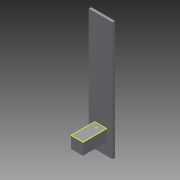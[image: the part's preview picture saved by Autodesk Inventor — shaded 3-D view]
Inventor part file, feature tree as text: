
AUTODESK INVENTOR PART (.ipt)
format: ipt  version: 2014 SP1 (Build 180222100, 222)  size: 95,232 bytes
history: native  units: in
note: dims shown in document units (in); Inventor stores cm internally (conversion verified against a paired STEP export)
features: sketch x4, extrude x2, hole x2
ambient origin geometry x8: Origin, YZ Plane, XZ Plane, XY Plane, X Axis, Y Axis, Z Axis, Center Point
bodies: Solid1 (feature_tree)
feature tree (8):
  extrude  "Extrusion1"  Depth=50.0in
  sketch  "Sketch2"  dims[d2=1.0in d3=0.0in d5=5.0in]
  hole  "Hole1"  [1 undecoded]
  extrude  "Extrusion2"  Depth=5.0in
  hole  "Hole2"  [1 undecoded]
  sketch  "Sketch4"  dims[d8=0.25in d9=0.75in d10=0.375in d11=0.25in d12=0.5635in d13=1.0in d14=0.8108in d15=10.0in d16=0.0in d17=8.0in d18=0.25in d19=0.75in d20=0.375in d21=0.25in d22=0.5635in d23=1.0in d24=0.8108in]
  sketch  "Sketch1"  dims[d0=10.0in d1=50.0in]
  sketch  "Sketch3"  dims[d6=5.0in d7=5.0in]
note: 2 required parameter values undecoded (feature->parameter linkage not recoverable at this tier; creation-order binding heuristic only, values carry confidence <= 0.55)
